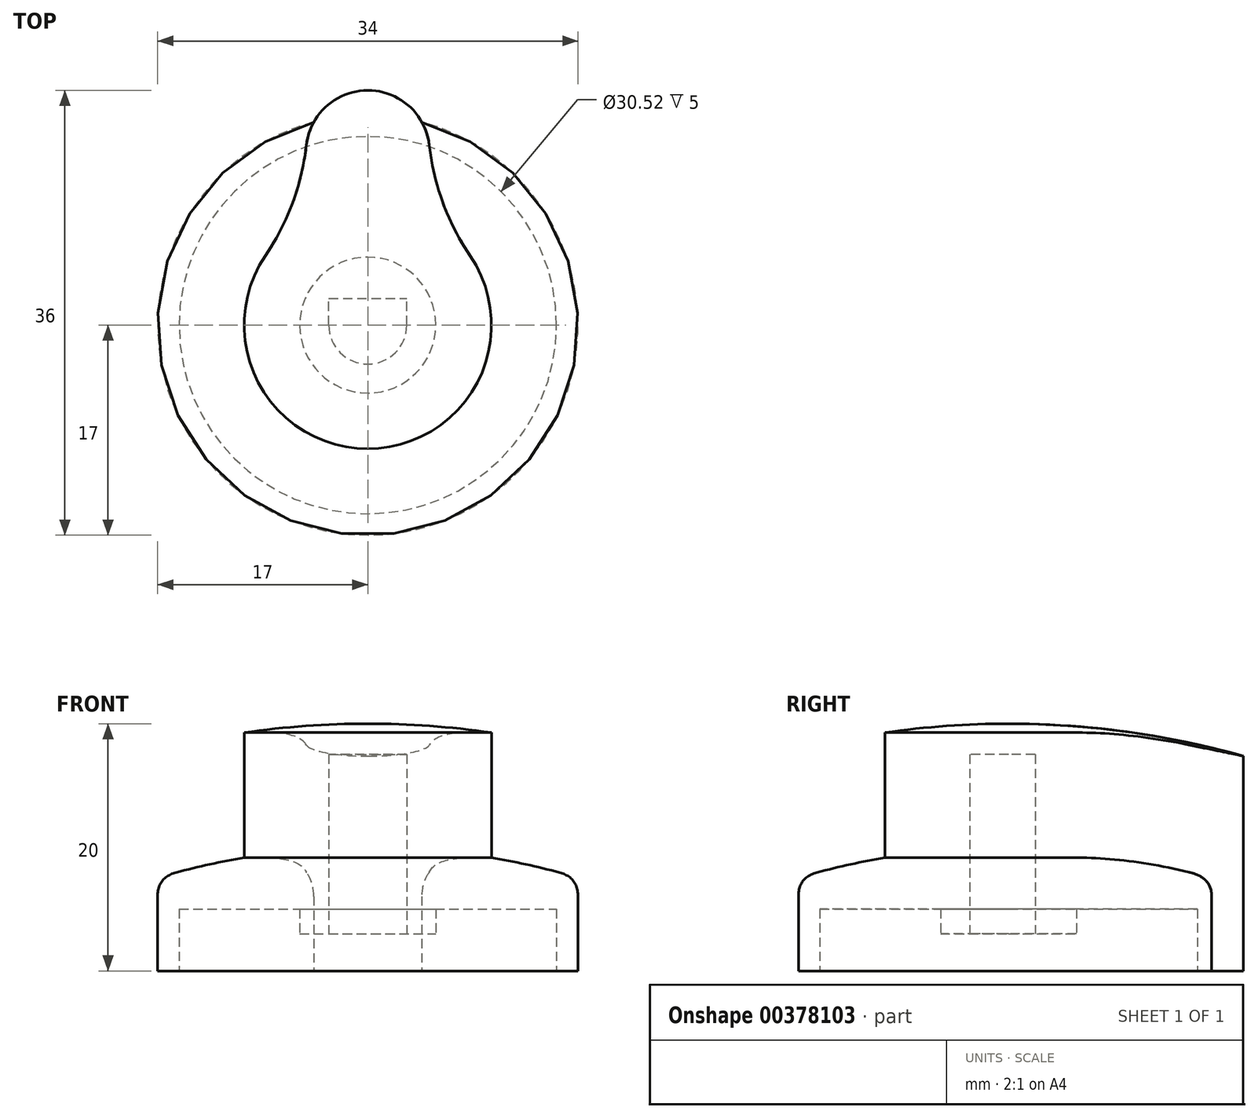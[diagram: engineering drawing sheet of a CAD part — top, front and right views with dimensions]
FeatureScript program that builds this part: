
annotation { "Feature Type Name" : "Feature", "Feature Type Description" : "" }
export const myFeature = defineFeature(function(context is Context, id is Id, definition is map)
    precondition{}
    {
        {
            var Q0;
            Q0=qCreatedBy(makeId("Right.planeOp"),FACE);
            var sketch = newSketch(context, id + "F0", { "sketchPlane" : qUnion([Q0])});
            skLineSegment(sketch, "E0", {"start": v(0, 0) * mm, "end": v(0, 10) * mm, "construction": true});
            skArc(sketch, "E1", {"start": v(17, 7.54) * mm, "mid": v(8.59, 9.38) * mm, "end": v(0, 10) * mm});
            skLineSegment(sketch, "E2", {"start": v(17, 7.54) * mm, "end": v(17, 0) * mm});
            skLineSegment(sketch, "E3", {"start": v(17, 0) * mm, "end": v(15.26, 0) * mm});
            skLineSegment(sketch, "E4", {"start": v(15.26, 0) * mm, "end": v(15.26, 5) * mm});
            skLineSegment(sketch, "E5", {"start": v(0, 3) * mm, "end": v(0, 10) * mm});
            skLineSegment(sketch, "E6", {"start": v(0, 10) * mm, "end": v(17, 10) * mm, "construction": true});
            skLineSegment(sketch, "E7", {"start": v(15.26, 0) * mm, "end": v(0, 0) * mm});
            skLineSegment(sketch, "E8", {"start": v(0, 3) * mm, "end": v(0, 0) * mm});
            skLineSegment(sketch, "E9", {"start": v(15.26, 5) * mm, "end": v(5.5, 5) * mm});
            skLineSegment(sketch, "E10", {"start": v(5.5, 5) * mm, "end": v(5.5, 3) * mm});
            skLineSegment(sketch, "E11", {"start": v(5.5, 3) * mm, "end": v(0, 3) * mm});
            skSolve(sketch);
        }
        {
            var Q0;
            Q0 = qSketchRegion(id + "F0", true);
            var Q1;
            Q1=sQuery(id+"F0.wireOp",EDGE,"E0");
            revolve(context, id + "F1", {"entities" : qUnion([Q0]), "axis" : qUnion([Q1]), "revolveType" : RevolveType.FULL});
        }
        {
            var Q0;
            Q0=makeQuery(id+"F1.opRevolve","SWEPT_FACE",FACE,{"disambiguationData":[OSD([sQuery(id+"F0.wireOp",EDGE,"E3"),sQuery(id+"F0.wireOp",EDGE,"E7")])]});
            var sketch = newSketch(context, id + "F2", { "sketchPlane" : qUnion([Q0])});
            skLineSegment(sketch, "E12", {"start": v(0, 0) * mm, "end": v(0, -17) * mm, "construction": true});
            skLineSegment(sketch, "E13", {"start": v(4.97, -14.56) * mm, "end": v(4.97, -14.56) * mm});
            skArc(sketch, "E14", {"start": v(8.28, -5.6) * mm, "mid": v(0, 10) * mm, "end": v(-8.28, -5.6) * mm});
            skArc(sketch, "E15", {"start": v(8.28, -5.6) * mm, "mid": v(6.08, -9.89) * mm, "end": v(4.97, -14.56) * mm});
            skArc(sketch, "E16.MirrorCS", {"start": v(-8.28, -5.6) * mm, "mid": v(-6.08, -9.89) * mm, "end": v(-4.97, -14.56) * mm});
            skCircle(sketch, "E17", {"center": v(0, -14) * mm, "radius": 3 * mm, "construction": true});
            skArc(sketch, "E18", {"start": v(-4.97, -14.56) * mm, "mid": v(0, -19) * mm, "end": v(4.97, -14.56) * mm});
            skSolve(sketch);
        }
        {
            var Q0;
            Q0 = qSketchRegion(id + "F2", true);
            extrude(context, id + "F3", {"entities" : qUnion([Q0]), "operationType" : NewBodyOperationType.ADD, "oppositeDirection" : true, "depth" : 20 * mm});
        }
        {
            var Q0;
            Q0=qCreatedBy(makeId("Right.planeOp"),FACE);
            var sketch = newSketch(context, id + "F4", { "sketchPlane" : qUnion([Q0])});
            skLineSegment(sketch, "E19", {"start": v(0, 0) * mm, "end": v(0, 20) * mm, "construction": true});
            skArc(sketch, "E20", {"start": v(20, 17.08) * mm, "mid": v(10.1, 19.27) * mm, "end": v(0, 20) * mm});
            skLineSegment(sketch, "E21", {"start": v(20, 17.08) * mm, "end": v(20, 21) * mm});
            skLineSegment(sketch, "E22", {"start": v(20, 21) * mm, "end": v(0, 21) * mm});
            skLineSegment(sketch, "E23", {"start": v(0, 21) * mm, "end": v(0, 20) * mm});
            skSolve(sketch);
        }
        {
            var Q0;
            Q0 = qSketchRegion(id + "F4", true);
            var Q1;
            Q1=sQuery(id+"F4.wireOp",EDGE,"E23");
            revolve(context, id + "F5", {"operationType" : NewBodyOperationType.REMOVE, "entities" : qUnion([Q0]), "axis" : qUnion([Q1]), "revolveType" : RevolveType.FULL, "oppositeDirection" : true});
        }
        {
            var Q0;
            Q0=makeQuery(id+"F0.imprint","IMPRINT",FACE,{"disambiguationData":[TD([[makeQuery(id+"F0.imprint","IMPRINT",EDGE,{"derivedFrom":sQuery(id+"F0.wireOp",EDGE,"E4")}),1.0]])]});
            var Q1;
            Q1=sQuery(id+"F0.wireOp",EDGE,"E8");
            revolve(context, id + "F6", {"operationType" : NewBodyOperationType.REMOVE, "entities" : qUnion([Q0]), "axis" : qUnion([Q1]), "revolveType" : RevolveType.FULL, "oppositeDirection" : true});
        }
        {
            var Q0;
            Q0=qCreatedBy(makeId("Top.planeOp"),FACE);
            var sketch = newSketch(context, id + "F7", { "sketchPlane" : qUnion([Q0])});
            skCircle(sketch, "E24", {"center": v(0, 0) * mm, "radius": 3.15 * mm, "construction": true});
            skLineSegment(sketch, "E25", {"start": v(3.15, 2.15) * mm, "end": v(-3.15, 2.15) * mm});
            skLineSegment(sketch, "E26", {"start": v(-3.15, 2.15) * mm, "end": v(-3.15, 0) * mm});
            skLineSegment(sketch, "E27", {"start": v(3.15, 2.15) * mm, "end": v(3.15, 0) * mm});
            skArc(sketch, "E28", {"start": v(-3.15, 0) * mm, "mid": v(0, -3.15) * mm, "end": v(3.15, 0) * mm});
            skLineSegment(sketch, "E29", {"start": v(3.15, -3.15) * mm, "end": v(-3.15, -3.15) * mm, "construction": true});
            skSolve(sketch);
        }
        {
            var Q0;
            Q0 = qSketchRegion(id + "F7", true);
            extrude(context, id + "F8", {"entities" : qUnion([Q0]), "operationType" : NewBodyOperationType.REMOVE, "depth" : 17.5 * mm});
        }
        {
            var Q0;
            Q0=makeQuery(id+"F1.opRevolve","SWEPT_EDGE",EDGE,{"disambiguationData":[OSD([sQuery(id+"F0.wireOp",EDGE,"E1"),sQuery(id+"F0.wireOp",EDGE,"d14a76e0-ef0d-4944-996e-54a5bd6425d80.MirrorCS")])]});
            fillet(context, id + "F9", {"entities" : qUnion([Q0]), "radius" : 2 * mm, "tangentPropagation" : true, "rho" : 0.5, "crossSection" : FilletCrossSection.CONIC, "allowEdgeOverflow" : false});
        }
    });
